# Revit family: Chair-Hussey-Quattro-Traditional-Classic-3D-Metric
name_source: partatom
category: Furniture
units: mm (PartAtom-declared; Revit-internal decimal feet)

## family parameters
Always vertical = Yes
Classification Number = 23.40.50.11.11.11
Cut with Voids When Loaded = No
Enable Cutting in Views = No
Render Appearance Source = Family Geometry
Room Calculation Point = No
Shared = No
Work Plane-Based = No

## types (1)
- Chair-Hussey-Quattro-Traditional-Classic-3D-Metric
    Armrest Finish = <By Category>
    Assembly Code = E2010500
    BIM Version = v3.1
    BIM Version Available (Earliest) = 2017
    CSI MasterFormat = 12 61 00
    Default Elevation = 0 mm
    Description = Quattro Traditional Collection
    Designer Guide = Refer to Product Selector Worksheet for all Options
    End Panel Finish = <By Category>
    Finish Options Website Link = http://204.239.146.105
    Floor Slope Angle = 0.00°
    Manufacturer = Hussey Seating Company
    Model = Quattro Traditional Collection
    Product Brochure PDF = http://www.hscedocs.com
    Product Page URL = http://www.husseyseating.com
    Product Selector Worksheet Link = http://www.husseyseating.com
    Quattro Literature Downloads = http://www.husseyseating.com
    Seat Back Angle = 21.00°
    Seat Back Angle Note = 12°, 15°, 18° or 21°
    Seat Back Finish = Hussey - Seat Pad - Generic
    Seat Back Outer Finish = <By Category>
    Seat Bottom Cover Finish = <By Category>
    Seat Pad Finish = Hussey - Seat Pad - Generic
    Seat Width Note = 500 mm, 525 mm, 550 mm, 575 mm, or 600 mm
    Series = Traditional - Classic
    Stanchion Finish = <By Category>
    URL = http://www.husseyseating.com

## geometry (parser evidence)
native form markers: Blend x11, Sweep x5
no freeform markers — native parametric forms only
